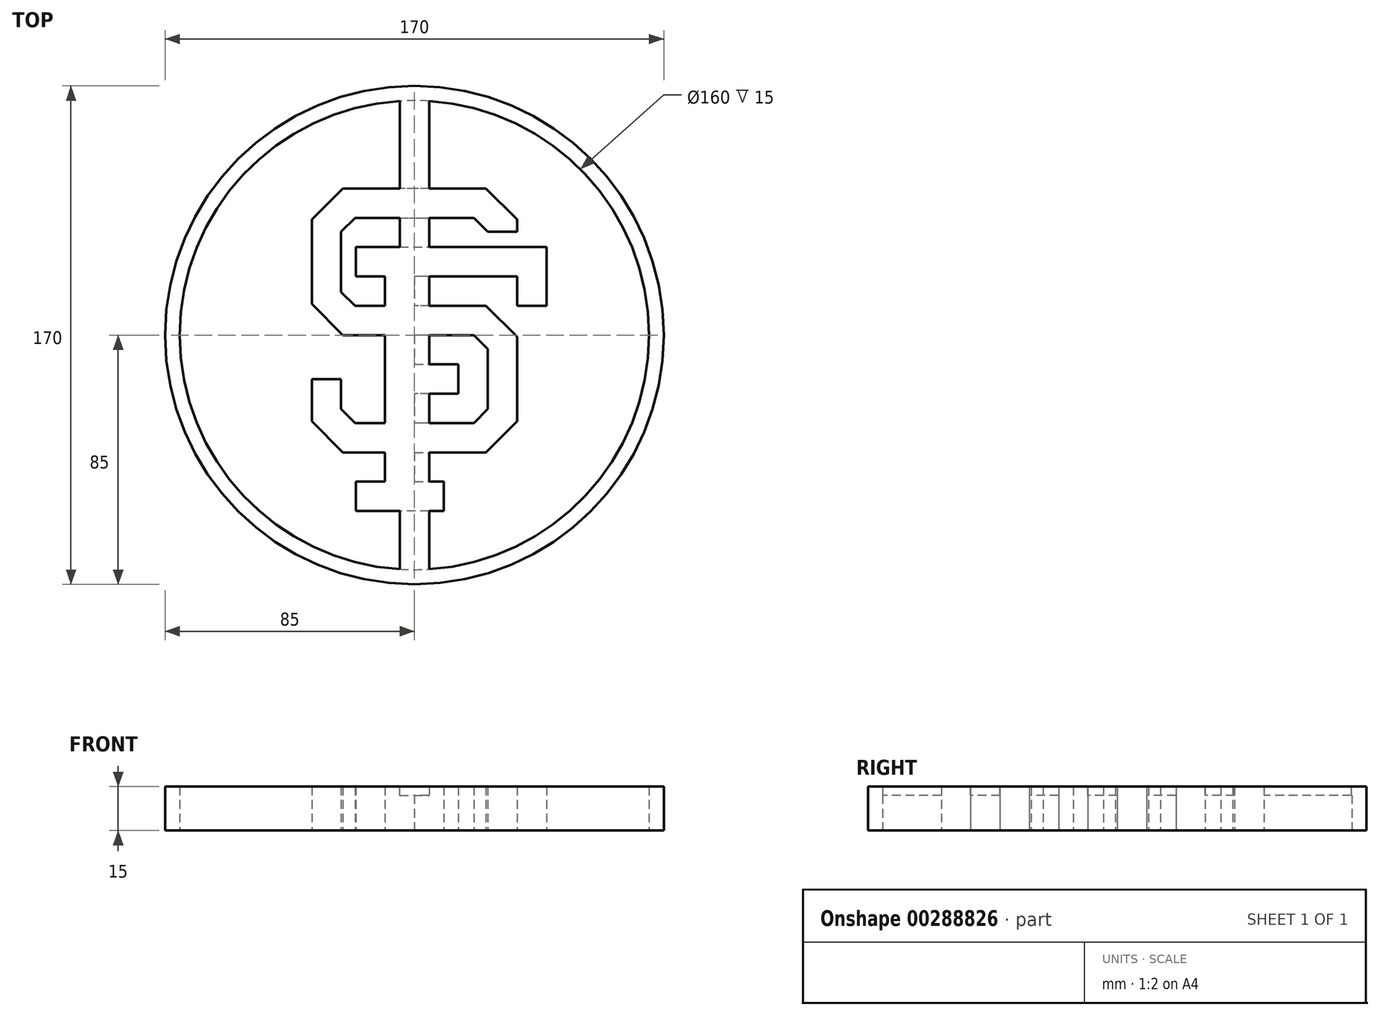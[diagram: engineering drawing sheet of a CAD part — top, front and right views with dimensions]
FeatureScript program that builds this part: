
annotation { "Feature Type Name" : "Feature", "Feature Type Description" : "" }
export const myFeature = defineFeature(function(context is Context, id is Id, definition is map)
    precondition{}
    {
        {
            var Q0;
            Q0=qCreatedBy(makeId("Top.planeOp"),FACE);
            var sketch = newSketch(context, id + "F0", { "sketchPlane" : qUnion([Q0])});
            skText(sketch, "E0", { "text": "S", "fontName": "DroidSansMono.ttf"});
            skLineSegment(sketch, "E1", {"start": v(-37.82, 0) * mm, "end": v(0, 0) * mm, "construction": true});
            const initialGuessF0  = {"E0": [-0.03782, -0.04, 1, 0, 0.08]};
            skSetInitialGuess(sketch, initialGuessF0);
            skSolve(sketch);
        }
        {
            var Q0;
            Q0=qCreatedBy(makeId("Top.planeOp"),FACE);
            var sketch = newSketch(context, id + "F1", { "sketchPlane" : qUnion([Q0])});
            skLineSegment(sketch, "E2", {"start": v(35, 39.4) * mm, "end": v(24.4, 50) * mm});
            skLineSegment(sketch, "E3", {"start": v(24.4, 50) * mm, "end": v(-24.4, 50) * mm});
            skLineSegment(sketch, "E4", {"start": v(-24.4, 50) * mm, "end": v(-35, 39.4) * mm});
            skLineSegment(sketch, "E5", {"start": v(-35, 39.4) * mm, "end": v(-35, 10.6) * mm});
            skLineSegment(sketch, "E6", {"start": v(20.25, 0) * mm, "end": v(25, -4.75) * mm});
            skLineSegment(sketch, "E7", {"start": v(25, -4.75) * mm, "end": v(25, -25.25) * mm});
            skLineSegment(sketch, "E8", {"start": v(25, -25.25) * mm, "end": v(20.25, -30) * mm});
            skLineSegment(sketch, "E9", {"start": v(20.25, -30) * mm, "end": v(-20.25, -30) * mm});
            skLineSegment(sketch, "E10", {"start": v(-20.25, -30) * mm, "end": v(-25, -25.25) * mm});
            skLineSegment(sketch, "E11", {"start": v(-25, -25.25) * mm, "end": v(-25, -15) * mm});
            skLineSegment(sketch, "E12", {"start": v(-25, -15) * mm, "end": v(-35, -15) * mm});
            skLineSegment(sketch, "E13", {"start": v(-35, -15) * mm, "end": v(-35, -29.4) * mm});
            skLineSegment(sketch, "E14", {"start": v(-35, -29.4) * mm, "end": v(-24.4, -40) * mm});
            skLineSegment(sketch, "E15", {"start": v(-24.4, -40) * mm, "end": v(24.4, -40) * mm});
            skLineSegment(sketch, "E16", {"start": v(24.4, -40) * mm, "end": v(35, -29.4) * mm});
            skLineSegment(sketch, "E17", {"start": v(35, -29.4) * mm, "end": v(35, -0.6) * mm});
            skLineSegment(sketch, "E18", {"start": v(35, -0.6) * mm, "end": v(24.4, 10) * mm});
            skLineSegment(sketch, "E19", {"start": v(24.4, 10) * mm, "end": v(-20.25, 10) * mm});
            skLineSegment(sketch, "E20", {"start": v(-25, 14.75) * mm, "end": v(-25, 35.25) * mm});
            skLineSegment(sketch, "E21", {"start": v(-25, 35.25) * mm, "end": v(-20.25, 40) * mm});
            skLineSegment(sketch, "E22", {"start": v(-20.25, 40) * mm, "end": v(20.25, 40) * mm});
            skLineSegment(sketch, "E23", {"start": v(20.25, 40) * mm, "end": v(25, 35.25) * mm});
            skLineSegment(sketch, "E24", {"start": v(25, 35.25) * mm, "end": v(35, 35.25) * mm});
            skLineSegment(sketch, "E25", {"start": v(35, 35.25) * mm, "end": v(35, 39.4) * mm});
            skLineSegment(sketch, "E26", {"start": v(-25, 14.75) * mm, "end": v(-20.25, 10) * mm});
            skLineSegment(sketch, "E27", {"start": v(20.25, 0) * mm, "end": v(-24.4, 0) * mm});
            skLineSegment(sketch, "E28", {"start": v(-24.4, 0) * mm, "end": v(-35, 10.6) * mm});
            skSolve(sketch);
        }
        {
            var Q0;
            Q0=qCreatedBy(makeId("Top.planeOp"),FACE);
            var sketch = newSketch(context, id + "F2", { "sketchPlane" : qUnion([Q0])});
            skLineSegment(sketch, "E29", {"start": v(-20, -60) * mm, "end": v(-20, -50) * mm});
            skLineSegment(sketch, "E30", {"start": v(-20, -50) * mm, "end": v(-10, -50) * mm});
            skLineSegment(sketch, "E31", {"start": v(-10, -50) * mm, "end": v(-10, 20) * mm});
            skLineSegment(sketch, "E32", {"start": v(-10, 20) * mm, "end": v(-20, 20) * mm});
            skLineSegment(sketch, "E33", {"start": v(-20, 20) * mm, "end": v(-20, 30) * mm});
            skLineSegment(sketch, "E34", {"start": v(-20, 30) * mm, "end": v(45, 30) * mm});
            skLineSegment(sketch, "E35", {"start": v(45, 30) * mm, "end": v(45, 10) * mm});
            skLineSegment(sketch, "E36", {"start": v(45, 10) * mm, "end": v(35, 10) * mm});
            skLineSegment(sketch, "E37", {"start": v(35, 10) * mm, "end": v(35, 20) * mm});
            skLineSegment(sketch, "E38", {"start": v(35, 20) * mm, "end": v(0, 20) * mm});
            skLineSegment(sketch, "E39", {"start": v(0, 20) * mm, "end": v(0, -10) * mm});
            skLineSegment(sketch, "E40", {"start": v(0, -10) * mm, "end": v(15, -10) * mm});
            skLineSegment(sketch, "E41", {"start": v(15, -10) * mm, "end": v(15, -20) * mm});
            skLineSegment(sketch, "E42", {"start": v(15, -20) * mm, "end": v(0, -20) * mm});
            skLineSegment(sketch, "E43", {"start": v(0, -20) * mm, "end": v(0, -50) * mm});
            skLineSegment(sketch, "E44", {"start": v(0, -50) * mm, "end": v(10, -50) * mm});
            skLineSegment(sketch, "E45", {"start": v(10, -50) * mm, "end": v(10, -60) * mm});
            skLineSegment(sketch, "E46", {"start": v(10, -60) * mm, "end": v(-20, -60) * mm});
            skSolve(sketch);
        }
        {
            var Q0;
            Q0=qCreatedBy(makeId("Top.planeOp"),FACE);
            var sketch = newSketch(context, id + "F3", { "sketchPlane" : qUnion([Q0])});
            skLineSegment(sketch, "E47.0", {"start": v(-24.4, 50) * mm, "end": v(-35, 39.4) * mm});
            skLineSegment(sketch, "E48.0", {"start": v(-35, 39.4) * mm, "end": v(-35, 10.6) * mm});
            skLineSegment(sketch, "E49.0", {"start": v(-10, -50) * mm, "end": v(-10, -40) * mm});
            skLineSegment(sketch, "E50.0", {"start": v(24.4, 10) * mm, "end": v(0, 10) * mm});
            skLineSegment(sketch, "E51.0", {"start": v(-25, 14.75) * mm, "end": v(-25, 35.25) * mm});
            skLineSegment(sketch, "E52.0", {"start": v(-25, 35.25) * mm, "end": v(-20.25, 40) * mm});
            skLineSegment(sketch, "E53.0", {"start": v(-20.25, 40) * mm, "end": v(20.25, 40) * mm});
            skPoint(sketch, "E54.0", {"position": v(22.63, 37.63) * mm});
            skPoint(sketch, "E55.0", {"position": v(25, 35.25) * mm});
            skLineSegment(sketch, "E56.0", {"start": v(20.25, 40) * mm, "end": v(25, 35.25) * mm});
            skLineSegment(sketch, "E57.0", {"start": v(25, 35.25) * mm, "end": v(35, 35.25) * mm});
            skLineSegment(sketch, "E58.0", {"start": v(35, 35.25) * mm, "end": v(35, 39.4) * mm});
            skLineSegment(sketch, "E59.0", {"start": v(35, 39.4) * mm, "end": v(24.4, 50) * mm});
            skLineSegment(sketch, "E60.0", {"start": v(24.4, 50) * mm, "end": v(-24.4, 50) * mm});
            skLineSegment(sketch, "E61.0", {"start": v(-10, 20) * mm, "end": v(-20, 20) * mm});
            skLineSegment(sketch, "E62.0", {"start": v(-20, 20) * mm, "end": v(-20, 30) * mm});
            skLineSegment(sketch, "E63.0", {"start": v(-20, 30) * mm, "end": v(45, 30) * mm});
            skLineSegment(sketch, "E64.0", {"start": v(45, 30) * mm, "end": v(45, 10) * mm});
            skLineSegment(sketch, "E65.0", {"start": v(45, 10) * mm, "end": v(35, 10) * mm});
            skLineSegment(sketch, "E66.0", {"start": v(35, 10) * mm, "end": v(35, 20) * mm});
            skLineSegment(sketch, "E67.0", {"start": v(35, 20) * mm, "end": v(0, 20) * mm});
            skLineSegment(sketch, "E68.0", {"start": v(0, 20) * mm, "end": v(0, 10) * mm});
            skLineSegment(sketch, "E69.0", {"start": v(35, -0.6) * mm, "end": v(24.4, 10) * mm});
            skLineSegment(sketch, "E70.0", {"start": v(25, -4.75) * mm, "end": v(25, -25.25) * mm});
            skLineSegment(sketch, "E71.0", {"start": v(20.25, 0) * mm, "end": v(25, -4.75) * mm});
            skLineSegment(sketch, "E72.0", {"start": v(35, -29.4) * mm, "end": v(35, -0.6) * mm});
            skLineSegment(sketch, "E73.0", {"start": v(15, -10) * mm, "end": v(15, -20) * mm});
            skLineSegment(sketch, "E74.0", {"start": v(0, -10) * mm, "end": v(15, -10) * mm});
            skLineSegment(sketch, "E75.0", {"start": v(15, -20) * mm, "end": v(0, -20) * mm});
            skLineSegment(sketch, "E76.0", {"start": v(0, -20) * mm, "end": v(0, -30) * mm});
            skLineSegment(sketch, "E77.0", {"start": v(20.25, -30) * mm, "end": v(0, -30) * mm});
            skLineSegment(sketch, "E78.0", {"start": v(25, -25.25) * mm, "end": v(20.25, -30) * mm});
            skLineSegment(sketch, "E79.0", {"start": v(24.4, -40) * mm, "end": v(35, -29.4) * mm});
            skLineSegment(sketch, "E80.0", {"start": v(-24.4, -40) * mm, "end": v(-10, -40) * mm});
            skLineSegment(sketch, "E81.0", {"start": v(0, -50) * mm, "end": v(10, -50) * mm});
            skLineSegment(sketch, "E82.0", {"start": v(10, -50) * mm, "end": v(10, -60) * mm});
            skLineSegment(sketch, "E83.0", {"start": v(10, -60) * mm, "end": v(-20, -60) * mm});
            skLineSegment(sketch, "E84.0", {"start": v(-20, -60) * mm, "end": v(-20, -50) * mm});
            skLineSegment(sketch, "E85.0", {"start": v(-20, -50) * mm, "end": v(-10, -50) * mm});
            skLineSegment(sketch, "E86.0", {"start": v(-35, -29.4) * mm, "end": v(-24.4, -40) * mm});
            skLineSegment(sketch, "E87.0", {"start": v(-35, -15) * mm, "end": v(-35, -29.4) * mm});
            skLineSegment(sketch, "E88.0.5", {"start": v(-35, 39.4) * mm, "end": v(-35, 39.4) * mm});
            skLineSegment(sketch, "E88.0.12", {"start": v(-20.25, -30) * mm, "end": v(-25, -25.25) * mm});
            skLineSegment(sketch, "E88.0.13", {"start": v(-25, -25.25) * mm, "end": v(-25, -15) * mm});
            skLineSegment(sketch, "E88.0.14", {"start": v(-25, -15) * mm, "end": v(-35, -15) * mm});
            skLineSegment(sketch, "E88.0.23", {"start": v(-25, 18.9) * mm, "end": v(-25, 35.25) * mm});
            skLineSegment(sketch, "E89.trimOffspring", {"start": v(-10, 10) * mm, "end": v(-20.25, 10) * mm});
            skLineSegment(sketch, "E90.trimOffspring", {"start": v(-10, 10) * mm, "end": v(-10, 20) * mm});
            skLineSegment(sketch, "E91.trimOffspring", {"start": v(0, 12.32) * mm, "end": v(0, 10) * mm});
            skLineSegment(sketch, "E92.trimOffspring", {"start": v(-10, -30) * mm, "end": v(-20.25, -30) * mm});
            skLineSegment(sketch, "E93.trimOffspring", {"start": v(0, -40) * mm, "end": v(0, -50) * mm});
            skLineSegment(sketch, "E94.trimOffspring", {"start": v(-10, -30) * mm, "end": v(-10, 0) * mm});
            skLineSegment(sketch, "E95.trimOffspring", {"start": v(0, -40) * mm, "end": v(24.4, -40) * mm});
            skLineSegment(sketch, "E96.0", {"start": v(-25, 14.75) * mm, "end": v(-20.25, 10) * mm});
            skLineSegment(sketch, "E97.0", {"start": v(-24.4, 0) * mm, "end": v(-35, 10.6) * mm});
            skLineSegment(sketch, "E98.0", {"start": v(20.25, 0) * mm, "end": v(0, 0) * mm});
            skLineSegment(sketch, "E99.trimOffspring", {"start": v(-10, 10) * mm, "end": v(-10, 18.4) * mm});
            skLineSegment(sketch, "E100.trimOffspring", {"start": v(-10, 0) * mm, "end": v(-24.4, 0) * mm});
            skLineSegment(sketch, "E101.trimOffspring", {"start": v(0, 0) * mm, "end": v(0, -10) * mm});
            skSolve(sketch);
        }
        {
            var Q0;
            Q0 = qSketchRegion(id + "F3", true);
            extrude(context, id + "F4", {"entities" : qUnion([Q0]), "depth" : 15 * mm});
        }
        {
            var Q0;
            Q0=qCreatedBy(makeId("Top.planeOp"),FACE);
            var sketch = newSketch(context, id + "F5", { "sketchPlane" : qUnion([Q0])});
            skCircle(sketch, "E102", {"center": v(0, 0) * mm, "radius": 80 * mm});
            skCircle(sketch, "E103", {"center": v(0, 0) * mm, "radius": 85 * mm});
            skSolve(sketch);
        }
        {
            var Q0;
            Q0 = qSketchRegion(id + "F5", true);
            extrude(context, id + "F6", {"entities" : qUnion([Q0]), "depth" : 15 * mm});
        }
        {
            var Q0;
            Q0=makeQuery(id+"F6.opExtrude","CAP_FACE",FACE,{"disambiguationData":[OSD([sQuery(id+"F5.wireOp",EDGE,"E102"),sQuery(id+"F5.wireOp",EDGE,"E103")])],"isStart":false});
            var sketch = newSketch(context, id + "F7", { "sketchPlane" : qUnion([Q0])});
            skLineSegment(sketch, "E104", {"start": v(-79.84, 5) * mm, "end": v(79.84, 5) * mm});
            skLineSegment(sketch, "E105", {"start": v(0, 0) * mm, "end": v(49.87, 0) * mm, "construction": true});
            skLineSegment(sketch, "E106.MirrorCS", {"start": v(-79.84, -5) * mm, "end": v(79.84, -5) * mm});
            skLineSegment(sketch, "E107", {"start": v(-5, 79.84) * mm, "end": v(-5, -79.84) * mm});
            skLineSegment(sketch, "E108", {"start": v(0, 0) * mm, "end": v(0, 55.7) * mm, "construction": true});
            skLineSegment(sketch, "E109.MirrorCS", {"start": v(5, 79.84) * mm, "end": v(5, -79.84) * mm});
            skSolve(sketch);
        }
        {
            var Q0;
            Q0 = qSketchRegion(id + "F7", true);
            var Q1;
            {var subQ0=sQuery(id+"F7.wireOp",EDGE,"E104");var subQ1=makeQuery(id+"F6.opExtrude","CAP_EDGE",EDGE,{"disambiguationData":[OSD([sQuery(id+"F5.wireOp",EDGE,"E102")])],"isStart":false});var subQ2=makeQuery(id+"F7.imprint","INTERSECT",VERTEX,{"disambiguationData":[OD(0.0)],"derivedFrom":[subQ1,subQ0]});Q1=makeQuery(id+"F7.imprint","IMPRINT",FACE,{"disambiguationData":[TD([[makeQuery(id+"F7.imprint","IMPRINT",EDGE,{"disambiguationData":[TD([[subQ2,-1.0]])],"derivedFrom":subQ0}),-1.0]])]});}
            var Q2;
            {var subQ0=sQuery(id+"F7.wireOp",EDGE,"E107");var subQ1=sQuery(id+"F7.wireOp",EDGE,"E104");var subQ2=makeQuery(id+"F7.imprint","INTERSECT",VERTEX,{"derivedFrom":[subQ1,subQ0]});Q2=makeQuery(id+"F7.imprint","IMPRINT",FACE,{"disambiguationData":[TD([[makeQuery(id+"F7.imprint","IMPRINT",EDGE,{"disambiguationData":[TD([[subQ2,-1.0]])],"derivedFrom":subQ1}),1.0]])]});}
            var Q3;
            {var subQ0=sQuery(id+"F7.wireOp",EDGE,"E104");var subQ1=makeQuery(id+"F6.opExtrude","CAP_EDGE",EDGE,{"disambiguationData":[OSD([sQuery(id+"F5.wireOp",EDGE,"E102")])],"isStart":false});var subQ2=makeQuery(id+"F7.imprint","INTERSECT",VERTEX,{"disambiguationData":[OD(1.0)],"derivedFrom":[subQ1,subQ0]});Q3=makeQuery(id+"F7.imprint","IMPRINT",FACE,{"disambiguationData":[TD([[makeQuery(id+"F7.imprint","IMPRINT",EDGE,{"disambiguationData":[TD([[subQ2,1.0]])],"derivedFrom":subQ0}),-1.0]])]});}
            var Q4;
            {var subQ0=sQuery(id+"F7.wireOp",EDGE,"E107");var subQ1=sQuery(id+"F7.wireOp",EDGE,"E106.MirrorCS");var subQ2=makeQuery(id+"F7.imprint","INTERSECT",VERTEX,{"derivedFrom":[subQ1,subQ0]});Q4=makeQuery(id+"F7.imprint","IMPRINT",FACE,{"disambiguationData":[TD([[makeQuery(id+"F7.imprint","IMPRINT",EDGE,{"disambiguationData":[TD([[subQ2,-1.0]])],"derivedFrom":subQ1}),-1.0]])]});}
            extrude(context, id + "F8", {"entities" : qUnion([Q0, Q1, Q2, Q3, Q4]), "operationType" : NewBodyOperationType.ADD, "oppositeDirection" : true, "depth" : 3 * mm});
        }
    });
